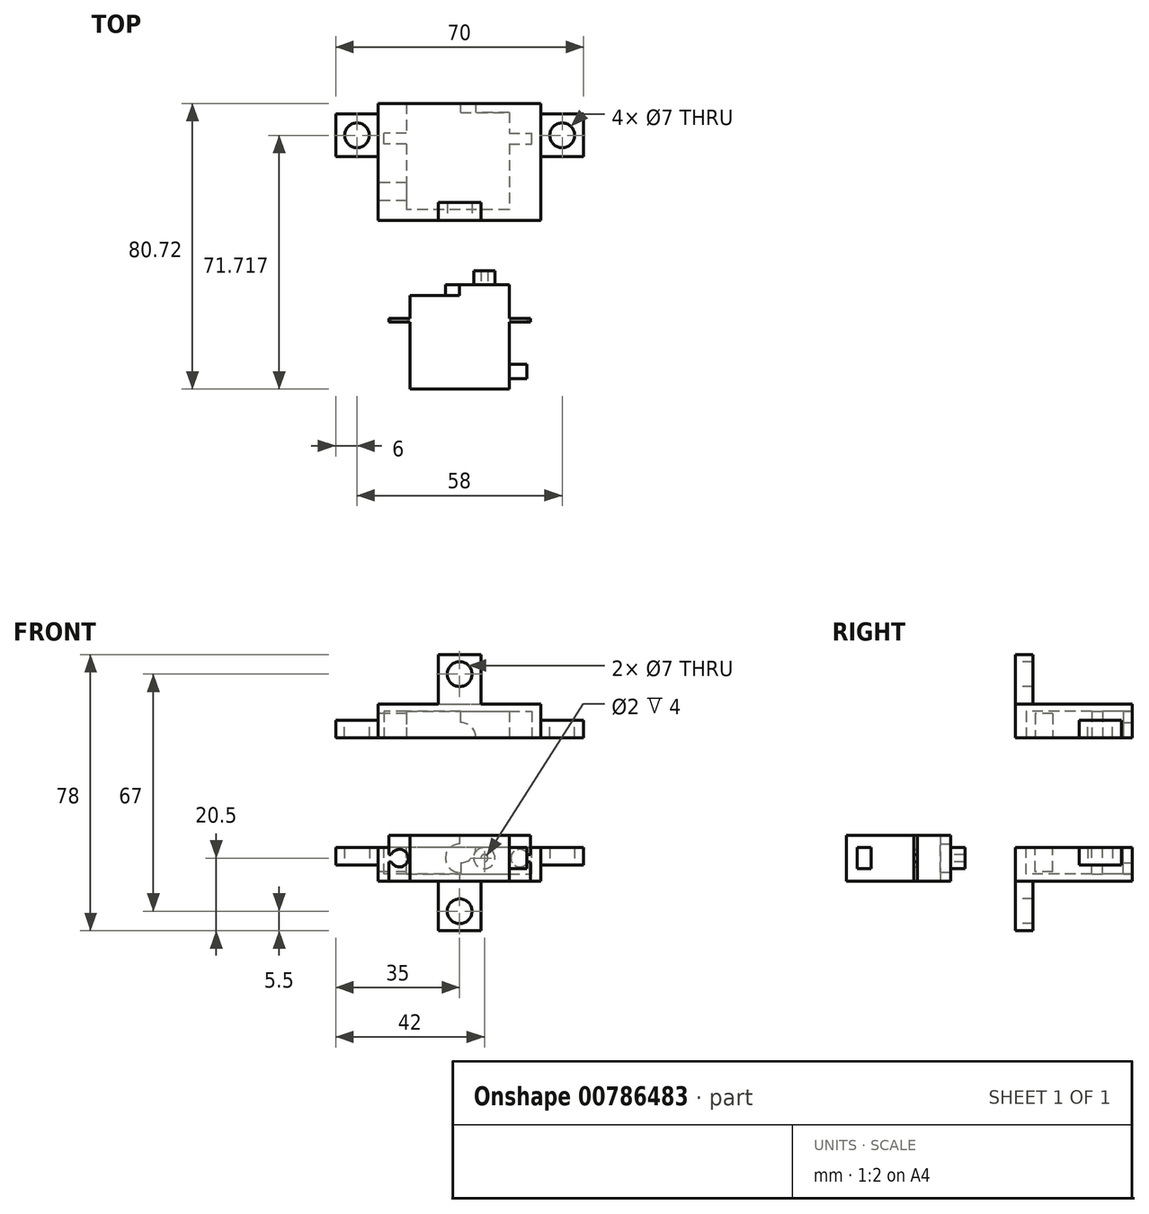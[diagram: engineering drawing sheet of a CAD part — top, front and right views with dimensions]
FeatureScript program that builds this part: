
annotation { "Feature Type Name" : "Feature", "Feature Type Description" : "" }
export const myFeature = defineFeature(function(context is Context, id is Id, definition is map)
    precondition{}
    {
        {
            var Q0;
            Q0=qCreatedBy(makeId("Top.planeOp"),FACE);
            var sketch = newSketch(context, id + "F0", { "sketchPlane" : qUnion([Q0])});
            skLineSegment(sketch, "E0.bottom", {"start": v(-14, 14.75) * mm, "end": v(14, 14.75) * mm});
            skLineSegment(sketch, "E0.top", {"start": v(-14, -14.75) * mm, "end": v(14, -14.75) * mm});
            skLineSegment(sketch, "E0.left", {"start": v(-14, 14.75) * mm, "end": v(-14, -14.75) * mm});
            skLineSegment(sketch, "E0.right", {"start": v(14, 14.75) * mm, "end": v(14, -14.75) * mm});
            skSolve(sketch);
        }
        {
            var Q0;
            Q0 = qSketchRegion(id + "F0", true);
            extrude(context, id + "F1", {"entities" : qUnion([Q0]), "depth" : 13 * mm, "offsetDistance" : 25 * mm});
        }
        {
            var Q0;
            Q0=makeQuery(id+"F1.opExtrude","SWEPT_FACE",FACE,{"disambiguationData":[OSD([sQuery(id+"F0.wireOp",EDGE,"E0.bottom")])]});
            var sketch = newSketch(context, id + "F2", { "sketchPlane" : qUnion([Q0])});
            skCircle(sketch, "E1", {"center": v(0, 6.5) * mm, "radius": 4 * mm});
            skPoint(sketch, "E1.centerSnap0", {"position": v(-14, 6.5) * mm});
            skLineSegment(sketch, "E2", {"start": v(0, 2.5) * mm, "end": v(0, 0) * mm});
            skLineSegment(sketch, "E3", {"start": v(0, 0) * mm, "end": v(14, 0) * mm});
            skLineSegment(sketch, "E4", {"start": v(14, 0) * mm, "end": v(14, 13) * mm});
            skLineSegment(sketch, "E5", {"start": v(14, 13) * mm, "end": v(0, 13) * mm});
            skLineSegment(sketch, "E6", {"start": v(0, 13) * mm, "end": v(0, 10.5) * mm});
            skSolve(sketch);
        }
        {
            var Q0;
            {var subQ0=sQuery(id+"F2.wireOp",EDGE,"E2");Q0=makeQuery(id+"F2.imprint","IMPRINT",FACE,{"disambiguationData":[TD([[makeQuery(id+"F2.imprint","IMPRINT",EDGE,{"derivedFrom":subQ0}),1.0]])]});}
            extrude(context, id + "F3", {"entities" : qUnion([Q0]), "operationType" : NewBodyOperationType.REMOVE, "oppositeDirection" : true, "depth" : 3 * mm, "offsetDistance" : 25 * mm});
        }
        {
            var Q0;
            Q0=makeQuery(id+"F1.opExtrude","SWEPT_FACE",FACE,{"disambiguationData":[OSD([sQuery(id+"F0.wireOp",EDGE,"E0.bottom")])]});
            var sketch = newSketch(context, id + "F4", { "sketchPlane" : qUnion([Q0])});
            skCircle(sketch, "E7", {"center": v(-7, 6.5) * mm, "radius": 3 * mm});
            skPoint(sketch, "E7.centerSnap0", {"position": v(-14, 6.5) * mm});
            skPoint(sketch, "E7.centerSnap1", {"position": v(-7, 13) * mm});
            skCircle(sketch, "E8", {"center": v(-7, 6.5) * mm, "radius": 1 * mm});
            skSolve(sketch);
        }
        {
            var Q0;
            Q0 = qSketchRegion(id + "F4", true);
            extrude(context, id + "F5", {"entities" : qUnion([Q0]), "operationType" : NewBodyOperationType.ADD, "depth" : 4 * mm, "offsetDistance" : 25 * mm});
        }
        {
            var Q0;
            Q0=makeQuery(id+"F1.opExtrude","SWEPT_FACE",FACE,{"disambiguationData":[OSD([sQuery(id+"F0.wireOp",EDGE,"E0.left")])]});
            var sketch = newSketch(context, id + "F6", { "sketchPlane" : qUnion([Q0])});
            skLineSegment(sketch, "E9.bottom", {"start": v(-5.25, 0) * mm, "end": v(-4.25, 0) * mm});
            skLineSegment(sketch, "E9.top", {"start": v(-5.25, 13) * mm, "end": v(-4.25, 13) * mm});
            skLineSegment(sketch, "E9.left", {"start": v(-5.25, 0) * mm, "end": v(-5.25, 13) * mm});
            skLineSegment(sketch, "E9.right", {"start": v(-4.25, 0) * mm, "end": v(-4.25, 13) * mm});
            skSolve(sketch);
        }
        {
            var Q0;
            Q0 = qSketchRegion(id + "F6", true);
            extrude(context, id + "F7", {"entities" : qUnion([Q0]), "operationType" : NewBodyOperationType.ADD, "depth" : 6 * mm, "offsetDistance" : 25 * mm});
        }
        {
            var Q0;
            Q0=makeQuery(id+"F1.opExtrude","SWEPT_FACE",FACE,{"disambiguationData":[OSD([sQuery(id+"F0.wireOp",EDGE,"E0.right")])]});
            var sketch = newSketch(context, id + "F8", { "sketchPlane" : qUnion([Q0])});
            skLineSegment(sketch, "E10.bottom", {"start": v(5.25, 13) * mm, "end": v(4.25, 13) * mm});
            skLineSegment(sketch, "E10.top", {"start": v(5.25, 0) * mm, "end": v(4.25, 0) * mm});
            skLineSegment(sketch, "E10.left", {"start": v(5.25, 13) * mm, "end": v(5.25, 0) * mm});
            skLineSegment(sketch, "E10.right", {"start": v(4.25, 13) * mm, "end": v(4.25, 0) * mm});
            skSolve(sketch);
        }
        {
            var Q0;
            Q0 = qSketchRegion(id + "F8", true);
            extrude(context, id + "F9", {"entities" : qUnion([Q0]), "operationType" : NewBodyOperationType.ADD, "depth" : 6 * mm, "offsetDistance" : 25 * mm});
        }
        {
            var Q0;
            Q0=makeQuery(id+"F9.opExtrude","SWEPT_FACE",FACE,{"disambiguationData":[OSD([sQuery(id+"F8.wireOp",EDGE,"E10.left")])]});
            var sketch = newSketch(context, id + "F10", { "sketchPlane" : qUnion([Q0])});
            skArc(sketch, "E11", {"start": v(-19.28, 5.5) * mm, "mid": v(-14.49, 6.5) * mm, "end": v(-19.28, 7.5) * mm});
            skLineSegment(sketch, "E12", {"start": v(-19.28, 5.5) * mm, "end": v(-20, 5.5) * mm});
            skLineSegment(sketch, "E13", {"start": v(-19.28, 7.5) * mm, "end": v(-20, 7.5) * mm});
            skSolve(sketch);
        }
        {
            var Q0;
            Q0=makeQuery(id+"F10.imprint","IMPRINT",FACE,{"disambiguationData":[TD([[makeQuery(id+"F10.imprint","IMPRINT",EDGE,{"derivedFrom":sQuery(id+"F10.wireOp",EDGE,"E11")}),1.0]])]});
            extrude(context, id + "F11", {"entities" : qUnion([Q0]), "operationType" : NewBodyOperationType.REMOVE, "oppositeDirection" : true, "depth" : 1 * mm, "offsetDistance" : 25 * mm});
        }
        {
            var Q0;
            Q0=makeQuery(id+"F7.opExtrude","SWEPT_FACE",FACE,{"disambiguationData":[OSD([sQuery(id+"F6.wireOp",EDGE,"E9.left")])]});
            var sketch = newSketch(context, id + "F12", { "sketchPlane" : qUnion([Q0])});
            skArc(sketch, "E14", {"start": v(19.3, 7.5) * mm, "mid": v(14.5, 6.5) * mm, "end": v(19.3, 5.5) * mm});
            skLineSegment(sketch, "E15", {"start": v(19.3, 5.5) * mm, "end": v(20, 5.5) * mm});
            skLineSegment(sketch, "E16", {"start": v(19.3, 7.5) * mm, "end": v(20, 7.5) * mm});
            skSolve(sketch);
        }
        {
            var Q0;
            Q0=makeQuery(id+"F12.imprint","IMPRINT",FACE,{"disambiguationData":[TD([[makeQuery(id+"F12.imprint","IMPRINT",EDGE,{"derivedFrom":sQuery(id+"F12.wireOp",EDGE,"E14")}),1.0]])]});
            extrude(context, id + "F13", {"entities" : qUnion([Q0]), "operationType" : NewBodyOperationType.REMOVE, "oppositeDirection" : true, "depth" : 1 * mm, "offsetDistance" : 25 * mm});
        }
        {
            var Q0;
            {var subQ0=sQuery(id+"F0.wireOp",EDGE,"E0.top");var subQ1=sQuery(id+"F0.wireOp",EDGE,"E0.right");Q0=makeQuery(id+"F9.boolean.opBoolean","SPLIT",FACE,{"disambiguationData":[TD([makeQuery(id+"F1.opExtrude","SWEPT_FACE",FACE,{"disambiguationData":[OSD([subQ0])]})])],"derivedFrom":makeQuery(id+"F1.opExtrude","SWEPT_FACE",FACE,{"disambiguationData":[OSD([subQ1])]})});}
            var sketch = newSketch(context, id + "F14", { "sketchPlane" : qUnion([Q0])});
            skLineSegment(sketch, "E17.bottom", {"start": v(-7.75, 9.5) * mm, "end": v(-11.75, 9.5) * mm});
            skLineSegment(sketch, "E17.top", {"start": v(-7.75, 3.5) * mm, "end": v(-11.75, 3.5) * mm});
            skLineSegment(sketch, "E17.left", {"start": v(-7.75, 9.5) * mm, "end": v(-7.75, 3.5) * mm});
            skLineSegment(sketch, "E17.right", {"start": v(-11.75, 9.5) * mm, "end": v(-11.75, 3.5) * mm});
            skSolve(sketch);
        }
        {
            var Q0;
            Q0 = qSketchRegion(id + "F14", true);
            extrude(context, id + "F15", {"entities" : qUnion([Q0]), "operationType" : NewBodyOperationType.ADD, "depth" : 5 * mm, "offsetDistance" : 25 * mm});
        }
        {
            var Q0;
            Q0=qCreatedBy(makeId("Top.planeOp"),FACE);
            var sketch = newSketch(context, id + "F16", { "sketchPlane" : qUnion([Q0])});
            skLineSegment(sketch, "E18.bottom", {"start": v(-23, 65.97) * mm, "end": v(23, 65.97) * mm});
            skLineSegment(sketch, "E18.top", {"start": v(-23, 32.97) * mm, "end": v(23, 32.97) * mm});
            skLineSegment(sketch, "E18.left", {"start": v(-23, 65.97) * mm, "end": v(-23, 32.97) * mm});
            skLineSegment(sketch, "E18.right", {"start": v(23, 65.97) * mm, "end": v(23, 32.97) * mm});
            skLineSegment(sketch, "E19.bottom", {"start": v(-6, 32.97) * mm, "end": v(6, 32.97) * mm});
            skLineSegment(sketch, "E19.top", {"start": v(-6, 37.97) * mm, "end": v(6, 37.97) * mm});
            skLineSegment(sketch, "E19.left", {"start": v(-6, 32.97) * mm, "end": v(-6, 37.97) * mm});
            skLineSegment(sketch, "E19.right", {"start": v(6, 32.97) * mm, "end": v(6, 37.97) * mm});
            skSolve(sketch);
        }
        {
            var Q0;
            {var subQ6=makeQuery(id+"F16.imprint","IMPRINT",EDGE,{"derivedFrom":sQuery(id+"F16.wireOp",EDGE,"E19.top")});Q0=qUnion([makeQuery(id+"F16.imprint","IMPRINT",FACE,{"disambiguationData":[TD([[makeQuery(id+"F16.imprint","IMPRINT",EDGE,{"derivedFrom":sQuery(id+"F16.wireOp",EDGE,"E18.bottom")}),-1.0]])]}),makeQuery(id+"F16.imprint","IMPRINT",FACE,{"disambiguationData":[TD([[subQ6,-1.0]])]})]);}
            extrude(context, id + "F17", {"entities" : qUnion([Q0]), "depth" : 19 * mm, "offsetDistance" : 25 * mm});
        }
        {
            var Q0;
            Q0=makeQuery(id+"F17.opExtrude","SWEPT_FACE",FACE,{"disambiguationData":[OSD([sQuery(id+"F16.wireOp",EDGE,"E18.top")])]});
            cPlane(context, id + "F18", {"entities" : qUnion([Q0]), "cplaneType" : CPlaneType.OFFSET, "offset" : 3 * mm, "oppositeDirection" : true, "width" : 150 * mm, "height" : 150 * mm});
        }
        {
            var Q0;
            Q0=qCreatedBy(id+"F18.planeOp",FACE);
            var sketch = newSketch(context, id + "F19", { "sketchPlane" : qUnion([Q0])});
            skLineSegment(sketch, "E20.bottom", {"start": v(-15, 2) * mm, "end": v(14, 2) * mm});
            skLineSegment(sketch, "E20.top", {"start": v(-15, 16) * mm, "end": v(14, 16) * mm});
            skLineSegment(sketch, "E20.left", {"start": v(-15, 2) * mm, "end": v(-15, 16) * mm});
            skLineSegment(sketch, "E20.right", {"start": v(14, 2) * mm, "end": v(14, 16) * mm});
            skSolve(sketch);
        }
        {
            var Q0;
            Q0 = qSketchRegion(id + "F19", true);
            extrude(context, id + "F20", {"entities" : qUnion([Q0]), "operationType" : NewBodyOperationType.REMOVE, "oppositeDirection" : true, "depth" : 26.5 * mm, "offsetDistance" : 25 * mm});
        }
        {
            var Q0;
            Q0=makeQuery(id+"F17.opExtrude","SWEPT_FACE",FACE,{"disambiguationData":[OSD([sQuery(id+"F16.wireOp",EDGE,"E18.left")])]});
            var sketch = newSketch(context, id + "F21", { "sketchPlane" : qUnion([Q0])});
            skLineSegment(sketch, "E21.bottom", {"start": v(-32.97, 9.5) * mm, "end": v(-65.97, 9.5) * mm});
            skLineSegment(sketch, "E21.top", {"start": v(-32.97, 19) * mm, "end": v(-65.97, 19) * mm});
            skLineSegment(sketch, "E21.left", {"start": v(-32.97, 9.5) * mm, "end": v(-32.97, 19) * mm});
            skLineSegment(sketch, "E21.right", {"start": v(-65.97, 9.5) * mm, "end": v(-65.97, 19) * mm});
            skSolve(sketch);
        }
        {
            var Q0;
            Q0 = qSketchRegion(id + "F21", true);
            extrude(context, id + "F22", {"entities" : qUnion([Q0]), "operationType" : NewBodyOperationType.REMOVE, "oppositeDirection" : true, "depth" : 46 * mm, "offsetDistance" : 25 * mm});
        }
        {
            var Q0;
            Q0=makeQuery(id+"F17.opExtrude","SWEPT_FACE",FACE,{"disambiguationData":[OSD([sQuery(id+"F16.wireOp",EDGE,"E18.bottom")])]});
            var sketch = newSketch(context, id + "F23", { "sketchPlane" : qUnion([Q0])});
            skArc(sketch, "E22", {"start": v(-4.6, 9.5) * mm, "mid": v(-3.34, 6.46) * mm, "end": v(-0.3, 5.2) * mm});
            skLineSegment(sketch, "E23", {"start": v(-0.3, 5.2) * mm, "end": v(-0.3, 2) * mm});
            skLineSegment(sketch, "E24", {"start": v(-0.3, 2) * mm, "end": v(15, 2) * mm});
            skLineSegment(sketch, "E25", {"start": v(15, 2) * mm, "end": v(15, 9.5) * mm});
            skLineSegment(sketch, "E26", {"start": v(15, 9.5) * mm, "end": v(4, 9.5) * mm});
            skSolve(sketch);
        }
        {
            var Q0;
            {var subQ0=sQuery(id+"F23.wireOp",EDGE,"Smb46ACP-U6bs-uDq2-RBba-JiRML71n13AM");Q0=makeQuery(id+"F23.imprint","IMPRINT",FACE,{"disambiguationData":[TD([[makeQuery(id+"F23.imprint","IMPRINT",EDGE,{"derivedFrom":subQ0}),-1.0]])]});}
            var Q1;
            {var subQ0=sQuery(id+"F23.wireOp",EDGE,"Smb46ACP-U6bs-uDq2-RBba-JiRML71n13AM");Q1=makeQuery(id+"F23.imprint","IMPRINT",FACE,{"disambiguationData":[TD([[makeQuery(id+"F23.imprint","IMPRINT",EDGE,{"derivedFrom":subQ0}),1.0]])]});}
            var Q2;
            {var subQ0=sQuery(id+"F23.wireOp",EDGE,"E23");Q2=makeQuery(id+"F23.imprint","IMPRINT",FACE,{"disambiguationData":[TD([[makeQuery(id+"F23.imprint","IMPRINT",EDGE,{"derivedFrom":subQ0}),1.0]])]});}
            extrude(context, id + "F24", {"entities" : qUnion([Q0, Q1, Q2]), "operationType" : NewBodyOperationType.REMOVE, "oppositeDirection" : true, "depth" : 4 * mm, "offsetDistance" : 25 * mm});
        }
        {
            var Q0;
            Q0=makeQuery(id+"F22.boolean.opBoolean","COPY",FACE,{"derivedFrom":makeQuery(id+"F22.opExtrude","SWEPT_FACE",FACE,{"disambiguationData":[OSD([sQuery(id+"F21.wireOp",EDGE,"E21.bottom")])]})});
            var sketch = newSketch(context, id + "F25", { "sketchPlane" : qUnion([Q0])});
            skLineSegment(sketch, "E27", {"start": v(-15, 57.57) * mm, "end": v(-21.4, 57.57) * mm});
            skLineSegment(sketch, "E28", {"start": v(-15, 54.57) * mm, "end": v(-21.4, 54.57) * mm});
            skLineSegment(sketch, "E29", {"start": v(-21.4, 54.57) * mm, "end": v(-21.4, 57.57) * mm});
            skLineSegment(sketch, "E30", {"start": v(14, 54.57) * mm, "end": v(20.4, 54.57) * mm});
            skLineSegment(sketch, "E31", {"start": v(14, 57.57) * mm, "end": v(20.4, 57.57) * mm});
            skLineSegment(sketch, "E32", {"start": v(20.4, 54.57) * mm, "end": v(20.4, 57.57) * mm});
            skSolve(sketch);
        }
        {
            var Q0;
            {var subQ0=sQuery(id+"F25.wireOp",EDGE,"E27");Q0=makeQuery(id+"F25.imprint","IMPRINT",FACE,{"disambiguationData":[TD([[makeQuery(id+"F25.imprint","IMPRINT",EDGE,{"derivedFrom":subQ0}),1.0]])]});}
            var Q1;
            {var subQ0=sQuery(id+"F25.wireOp",EDGE,"E30");Q1=makeQuery(id+"F25.imprint","IMPRINT",FACE,{"disambiguationData":[TD([[makeQuery(id+"F25.imprint","IMPRINT",EDGE,{"derivedFrom":subQ0}),1.0]])]});}
            extrude(context, id + "F26", {"entities" : qUnion([Q0, Q1]), "operationType" : NewBodyOperationType.REMOVE, "oppositeDirection" : true, "depth" : 7.5 * mm, "offsetDistance" : 25 * mm});
        }
        {
            var Q0;
            Q0=makeQuery(id+"F22.boolean.opBoolean","COPY",FACE,{"derivedFrom":makeQuery(id+"F22.opExtrude","SWEPT_FACE",FACE,{"disambiguationData":[OSD([sQuery(id+"F21.wireOp",EDGE,"E21.bottom")])]})});
            var sketch = newSketch(context, id + "F27", { "sketchPlane" : qUnion([Q0])});
            skLineSegment(sketch, "E33.bottom", {"start": v(-15, 38.57) * mm, "end": v(-24, 38.57) * mm});
            skLineSegment(sketch, "E33.top", {"start": v(-15, 43.57) * mm, "end": v(-24, 43.57) * mm});
            skLineSegment(sketch, "E33.left", {"start": v(-15, 38.57) * mm, "end": v(-15, 43.57) * mm});
            skLineSegment(sketch, "E33.right", {"start": v(-24, 38.57) * mm, "end": v(-24, 43.57) * mm});
            skSolve(sketch);
        }
        {
            var Q0;
            Q0 = qSketchRegion(id + "F27", true);
            extrude(context, id + "F28", {"entities" : qUnion([Q0]), "operationType" : NewBodyOperationType.REMOVE, "oppositeDirection" : true, "depth" : 6.8 * mm, "offsetDistance" : 25 * mm});
        }
        {
            var Q0;
            Q0=makeQuery(id+"F16.imprint","IMPRINT",FACE,{"disambiguationData":[TD([[makeQuery(id+"F16.imprint","IMPRINT",EDGE,{"derivedFrom":sQuery(id+"F16.wireOp",EDGE,"E18.bottom")}),-1.0]])]});
            cPlane(context, id + "F29", {"entities" : qUnion([Q0]), "cplaneType" : CPlaneType.OFFSET, "offset" : 25 * mm, "width" : 150 * mm, "height" : 150 * mm});
        }
        {
            var Q0;
            Q0=makeQuery(id+"F17.opExtrude","SWEPT_BODY",BODY,{"disambiguationData":[OSD([sQuery(id+"F16.wireOp",EDGE,"E18.bottom"),sQuery(id+"F16.wireOp",EDGE,"E18.top"),sQuery(id+"F16.wireOp",EDGE,"E18.left"),sQuery(id+"F16.wireOp",EDGE,"E18.right")])]});
            transform(context, id + "F30", {"entities" : qUnion([Q0]), "transformType" : TransformType.TRANSLATION_3D, "dx" : 0 * mm, "dy" : 0 * mm, "dz" : 0 * mm, "makeCopy" : true});
        }
        {
            var Q0;
            Q0=makeQuery(id+"F17.opExtrude","SWEPT_FACE",FACE,{"disambiguationData":[OSD([sQuery(id+"F16.wireOp",EDGE,"E18.right")])]});
            var sketch = newSketch(context, id + "F31", { "sketchPlane" : qUnion([Q0])});
            skLineSegment(sketch, "E34.bottom", {"start": v(50.97, 9.5) * mm, "end": v(62.97, 9.5) * mm});
            skLineSegment(sketch, "E34.top", {"start": v(50.97, 4.5) * mm, "end": v(62.97, 4.5) * mm});
            skLineSegment(sketch, "E34.left", {"start": v(50.97, 9.5) * mm, "end": v(50.97, 4.5) * mm});
            skLineSegment(sketch, "E34.right", {"start": v(62.97, 9.5) * mm, "end": v(62.97, 4.5) * mm});
            skSolve(sketch);
        }
        {
            var Q0;
            Q0 = qSketchRegion(id + "F31", true);
            extrude(context, id + "F32", {"entities" : qUnion([Q0]), "operationType" : NewBodyOperationType.ADD, "depth" : 12 * mm, "offsetDistance" : 25 * mm});
        }
        {
            var Q0;
            Q0=makeQuery(id+"F17.opExtrude","SWEPT_FACE",FACE,{"disambiguationData":[OSD([sQuery(id+"F16.wireOp",EDGE,"E18.left")])]});
            var sketch = newSketch(context, id + "F33", { "sketchPlane" : qUnion([Q0])});
            skLineSegment(sketch, "E35.bottom", {"start": v(-50.97, 9.5) * mm, "end": v(-62.97, 9.5) * mm});
            skLineSegment(sketch, "E35.top", {"start": v(-50.97, 4.5) * mm, "end": v(-62.97, 4.5) * mm});
            skLineSegment(sketch, "E35.left", {"start": v(-50.97, 9.5) * mm, "end": v(-50.97, 4.5) * mm});
            skLineSegment(sketch, "E35.right", {"start": v(-62.97, 9.5) * mm, "end": v(-62.97, 4.5) * mm});
            skSolve(sketch);
        }
        {
            var Q0;
            Q0 = qSketchRegion(id + "F33", true);
            extrude(context, id + "F34", {"entities" : qUnion([Q0]), "operationType" : NewBodyOperationType.ADD, "depth" : 12 * mm, "offsetDistance" : 25 * mm});
        }
        {
            var Q0;
            Q0=makeQuery(id+"F34.opExtrude","SWEPT_FACE",FACE,{"disambiguationData":[OSD([sQuery(id+"F33.wireOp",EDGE,"E35.top")])]});
            var sketch = newSketch(context, id + "F35", { "sketchPlane" : qUnion([Q0])});
            skCircle(sketch, "E36", {"center": v(-29, -56.97) * mm, "radius": 3.5 * mm});
            skPoint(sketch, "E36.centerSnap0", {"position": v(-29, -50.97) * mm});
            skPoint(sketch, "E36.centerSnap1", {"position": v(-35, -56.97) * mm});
            skSolve(sketch);
        }
        {
            var Q0;
            Q0 = qSketchRegion(id + "F35", true);
            extrude(context, id + "F36", {"entities" : qUnion([Q0]), "operationType" : NewBodyOperationType.REMOVE, "oppositeDirection" : true, "depth" : 5 * mm, "offsetDistance" : 25 * mm});
        }
        {
            var Q0;
            Q0=makeQuery(id+"F32.opExtrude","SWEPT_FACE",FACE,{"disambiguationData":[OSD([sQuery(id+"F31.wireOp",EDGE,"E34.top")])]});
            var sketch = newSketch(context, id + "F37", { "sketchPlane" : qUnion([Q0])});
            skCircle(sketch, "E37", {"center": v(29, -56.97) * mm, "radius": 3.5 * mm});
            skPoint(sketch, "E37.centerSnap0", {"position": v(29, -50.97) * mm});
            skPoint(sketch, "E37.centerSnap1", {"position": v(35, -56.97) * mm});
            skSolve(sketch);
        }
        {
            var Q0;
            Q0 = qSketchRegion(id + "F37", true);
            extrude(context, id + "F38", {"entities" : qUnion([Q0]), "operationType" : NewBodyOperationType.REMOVE, "oppositeDirection" : true, "depth" : 5 * mm, "offsetDistance" : 25 * mm});
        }
        {
            var Q0;
            Q0=makeQuery(id+"F20.boolean.opBoolean","COPY",FACE,{"derivedFrom":makeQuery(id+"F20.opExtrude","CAP_FACE",FACE,{"disambiguationData":[OSD([sQuery(id+"F19.wireOp",EDGE,"E20.bottom"),sQuery(id+"F19.wireOp",EDGE,"E20.top"),sQuery(id+"F19.wireOp",EDGE,"E20.left"),sQuery(id+"F19.wireOp",EDGE,"E20.right")])],"isStart":false})});
            extrude(context, id + "F39", {"entities" : qUnion([Q0]), "operationType" : NewBodyOperationType.REMOVE, "oppositeDirection" : true, "depth" : 1 * mm, "offsetDistance" : 25 * mm});
        }
        {
            var Q0;
            Q0=makeQuery(id+"F16.imprint","IMPRINT",FACE,{"disambiguationData":[TD([[makeQuery(id+"F16.imprint","IMPRINT",EDGE,{"derivedFrom":sQuery(id+"F16.wireOp",EDGE,"E19.top")}),-1.0]])]});
            extrude(context, id + "F40", {"entities" : qUnion([Q0]), "operationType" : NewBodyOperationType.ADD, "oppositeDirection" : true, "depth" : 14 * mm, "offsetDistance" : 25 * mm});
        }
        {
            var Q0;
            {var subQ0=sQuery(id+"F16.wireOp",EDGE,"E18.top");Q0=makeQuery(id+"F40.boolean.opBoolean","MERGE",FACE,{"derivedFrom":[makeQuery(id+"F17.opExtrude","SWEPT_FACE",FACE,{"disambiguationData":[OSD([subQ0])]}),makeQuery(id+"F40.opExtrude","SWEPT_FACE",FACE,{"disambiguationData":[OSD([subQ0])]})]});}
            var sketch = newSketch(context, id + "F41", { "sketchPlane" : qUnion([Q0])});
            skCircle(sketch, "E38", {"center": v(0, -8.5) * mm, "radius": 3.5 * mm});
            skPoint(sketch, "E38.centerSnap0", {"position": v(0, -14) * mm});
            skPoint(sketch, "E38.centerSnap1", {"position": v(-6, -8.5) * mm});
            skSolve(sketch);
        }
        {
            var Q0;
            Q0 = qSketchRegion(id + "F41", true);
            extrude(context, id + "F42", {"entities" : qUnion([Q0]), "operationType" : NewBodyOperationType.REMOVE, "oppositeDirection" : true, "depth" : 5 * mm, "offsetDistance" : 25 * mm});
        }
        {
            var Q0;
            Q0=makeQuery(id+"F17.opExtrude","SWEPT_BODY",BODY,{"disambiguationData":[OSD([sQuery(id+"F16.wireOp",EDGE,"E18.bottom"),sQuery(id+"F16.wireOp",EDGE,"E18.top"),sQuery(id+"F16.wireOp",EDGE,"E18.left"),sQuery(id+"F16.wireOp",EDGE,"E18.right")])]});
            var Q1;
            Q1=qCreatedBy(id+"F29.planeOp",FACE);
            mirror(context, id + "F43", {"entities" : qUnion([Q0]), "mirrorPlane" : qUnion([Q1])});
        }
    });
